annotation { "Feature Type Name" : "Feature", "Feature Type Description" : "" }
export const myFeature = defineFeature(function(context is Context, id is Id, definition is map)
    precondition{}
    {
        {
            var Q0;
            Q0=qCreatedBy(makeId("Top.planeOp"),FACE);
            var sketch = newSketch(context, id + "F0", { "sketchPlane" : qUnion([Q0])});
            skLineSegment(sketch, "E0.bottom", {"start": v(-43.82, 31.44) * mm, "end": v(43.82, 31.44) * mm});
            skLineSegment(sketch, "E0.top", {"start": v(-43.82, -31.44) * mm, "end": v(43.82, -31.44) * mm});
            skLineSegment(sketch, "E0.left", {"start": v(-48.82, 26.44) * mm, "end": v(-48.82, -26.44) * mm});
            skLineSegment(sketch, "E0.right", {"start": v(48.82, 26.44) * mm, "end": v(48.82, -26.44) * mm});
            skPoint(sketch, "E0.middle", {"position": v(0, 0) * mm});
            skPoint(sketch, "E1.visualSharp", {"position": v(-48.82, 31.44) * mm});
            skArc(sketch, "E1.filletArc", {"start": v(-43.82, 31.44) * mm, "mid": v(-47.36, 29.97) * mm, "end": v(-48.82, 26.44) * mm});
            skPoint(sketch, "E2.visualSharp", {"position": v(-48.82, -31.44) * mm});
            skArc(sketch, "E2.filletArc", {"start": v(-48.82, -26.44) * mm, "mid": v(-47.36, -29.97) * mm, "end": v(-43.82, -31.44) * mm});
            skPoint(sketch, "E3.visualSharp", {"position": v(48.82, -31.44) * mm});
            skArc(sketch, "E3.filletArc", {"start": v(43.82, -31.44) * mm, "mid": v(47.36, -29.97) * mm, "end": v(48.82, -26.44) * mm});
            skPoint(sketch, "E4.visualSharp", {"position": v(48.82, 31.44) * mm});
            skArc(sketch, "E4.filletArc", {"start": v(48.82, 26.44) * mm, "mid": v(47.36, 29.97) * mm, "end": v(43.82, 31.44) * mm});
            skCircle(sketch, "E5", {"center": v(42.82, 25.44) * mm, "radius": 2.5 * mm});
            skCircle(sketch, "E6.MirrorC", {"center": v(-42.82, 25.44) * mm, "radius": 2.5 * mm});
            skSolve(sketch);
        }
        {
            var Q0;
            Q0 = qSketchRegion(id + "F0", true);
            extrude(context, id + "F1", {"entities" : qUnion([Q0]), "depth" : 3 * mm});
        }
        {
            var Q0;
            Q0=qCreatedBy(makeId("Top.planeOp"),FACE);
            var sketch = newSketch(context, id + "F2", { "sketchPlane" : qUnion([Q0])});
            skFitSpline(sketch, "E7", {"points": [v(21.62, 6.78) * mm, v(22.6, 7.89) * mm, v(23.46, 8.32) * mm, v(24.65, 8.86) * mm, v(25.98, 9.48) * mm, v(26.54, 10.02) * mm, v(26.92, 10.91) * mm, v(26.9, 11.43) * mm, v(26.65, 11.21) * mm, v(26.52, 11.4) * mm, v(27.08, 12.22) * mm, v(27.82, 12.98) * mm, v(27.9, 13.86) * mm, v(27.94, 15.05) * mm, v(27.94, 17.07) * mm, v(27.87, 17.63) * mm, v(27.9, 19.67) * mm, v(27.9, 21.6) * mm, v(28.27, 21.58) * mm, v(29.33, 20.23) * mm, v(31.93, 16.98) * mm, v(33.27, 15.72) * mm, v(34.13, 15.63) * mm, v(34.94, 16.39) * mm, v(36.1, 18.95) * mm, v(38, 21.24) * mm, v(39.47, 22.14) * mm, v(40.25, 21.06) * mm, v(40.25, 16.6) * mm, v(40, 15.33) * mm, v(40.39, 12.67) * mm, v(40.48, 11.3) * mm, v(40.1, 10.54) * mm, v(40.46, 9.74) * mm, v(41.2, 8.63) * mm, v(41.19, 5.67) * mm, v(40.78, 4.58) * mm, v(40.75, 3.15) * mm, v(41.2, 1.54) * mm, v(41.32, 0) * mm, v(41.23, -0.83) * mm, v(41.5, -3.03) * mm, v(42.07, -4.62) * mm, v(41.3, -4.92) * mm, v(40.39, -4.74) * mm, v(39.23, -5.24) * mm, v(38.64, -5.83) * mm, v(36.5, -6.12) * mm, v(35.75, -6.76) * mm, v(33.7, -6.83) * mm, v(32.03, -7.03) * mm, v(28.7, -5.96) * mm, v(25.46, -5.24) * mm, v(24.82, -4.5) * mm, v(25.03, -3.28) * mm, v(25.66, -1) * mm, v(26.16, 0.95) * mm, v(25.91, 1.17) * mm, v(25.53, 0.8) * mm, v(24.3, 1.01) * mm, v(24.35, 2.74) * mm, v(24.85, 3.6) * mm, v(24.8, 3.92) * mm, v(23.19, 3.92) * mm, v(22.07, 5.6) * mm, v(21.73, 5.85) * mm, v(21.62, 6.78) * mm]});
            skSolve(sketch);
        }
        {
            var Q0;
            Q0 = qSketchRegion(id + "F2", true);
            extrude(context, id + "F3", {"entities" : qUnion([Q0]), "depth" : 4 * mm});
        }
        {
            var Q0;
            Q0=qCreatedBy(makeId("Top.planeOp"),FACE);
            var sketch = newSketch(context, id + "F4", { "sketchPlane" : qUnion([Q0])});
            skText(sketch, "E8", { "text": "PO VSTUPE\nSA TI HNED\nBUDEM VENOVAT", "fontName": "AllertaStencil-Regular.ttf"});
            const initialGuessF4  = {"E8": [-0.04382, 0.0064, 1, 0, 0.00703]};
            skSetInitialGuess(sketch, initialGuessF4);
            skSolve(sketch);
        }
        {
            var Q0;
            Q0 = qSketchRegion(id + "F4", true);
            extrude(context, id + "F5", {"entities" : qUnion([Q0]), "operationType" : NewBodyOperationType.REMOVE, "depth" : 25 * mm});
        }
        {
            var Q0;
            Q0=makeQuery(id+"F3.opExtrude","SWEPT_BODY",BODY,{"disambiguationData":[OSD([sQuery(id+"F2.wireOp",EDGE,"E7")])]});
            transform(context, id + "F6", {"entities" : qUnion([Q0]), "transformType" : TransformType.TRANSLATION_3D, "dx" : 0 * mm, "dy" : 0 * mm, "dz" : 0 * mm, "makeCopy" : true});
        }
        {
            var Q0;
            Q0=makeQuery(id+"F6.opPattern","COPY",BODY,{"derivedFrom":makeQuery(id+"F3.opExtrude","SWEPT_BODY",BODY,{"disambiguationData":[OSD([sQuery(id+"F2.wireOp",EDGE,"E7")])]}),"instanceName":"1"});
            var Q1;
            Q1=makeQuery(id+"F1.opExtrude","CAP_EDGE",EDGE,{"disambiguationData":[OSD([sQuery(id+"F0.wireOp",EDGE,"E0.right")])],"isStart":false});
            transform(context, id + "F7", {"entities" : qUnion([Q0]), "transformType" : TransformType.ROTATION, "transformAxis" : qUnion([Q1]), "angle" : 1.7 * degree, "oppositeDirection" : true, "makeCopy" : false});
        }
        {
            var Q0;
            Q0=qCreatedBy(makeId("Top.planeOp"),FACE);
            var sketch = newSketch(context, id + "F8", { "sketchPlane" : qUnion([Q0])});
            skLineSegment(sketch, "E9.bottom", {"start": v(-42.32, 29.94) * mm, "end": v(42.32, 29.94) * mm});
            skLineSegment(sketch, "E9.top", {"start": v(-42.32, -29.94) * mm, "end": v(42.32, -29.94) * mm});
            skLineSegment(sketch, "E9.left", {"start": v(-47.32, 24.94) * mm, "end": v(-47.32, -24.94) * mm});
            skLineSegment(sketch, "E9.right", {"start": v(47.32, 24.94) * mm, "end": v(47.32, -24.94) * mm});
            skPoint(sketch, "E9.middle", {"position": v(0, 0) * mm});
            skPoint(sketch, "E10.visualSharp", {"position": v(-47.32, 29.94) * mm});
            skArc(sketch, "E10.filletArc", {"start": v(-42.32, 29.94) * mm, "mid": v(-45.86, 28.47) * mm, "end": v(-47.32, 24.94) * mm});
            skPoint(sketch, "E11.visualSharp", {"position": v(-47.32, -29.94) * mm});
            skArc(sketch, "E11.filletArc", {"start": v(-47.32, -24.94) * mm, "mid": v(-45.86, -28.47) * mm, "end": v(-42.32, -29.94) * mm});
            skPoint(sketch, "E12.visualSharp", {"position": v(47.32, -29.94) * mm});
            skArc(sketch, "E12.filletArc", {"start": v(42.32, -29.94) * mm, "mid": v(45.86, -28.47) * mm, "end": v(47.32, -24.94) * mm});
            skPoint(sketch, "E13.visualSharp", {"position": v(47.32, 29.94) * mm});
            skArc(sketch, "E13.filletArc", {"start": v(47.32, 24.94) * mm, "mid": v(45.86, 28.47) * mm, "end": v(42.32, 29.94) * mm});
            skLineSegment(sketch, "E14.bottom", {"start": v(-41.32, 28.94) * mm, "end": v(41.32, 28.94) * mm});
            skLineSegment(sketch, "E14.top", {"start": v(-41.32, -28.94) * mm, "end": v(41.32, -28.94) * mm});
            skLineSegment(sketch, "E14.left", {"start": v(-46.32, 23.94) * mm, "end": v(-46.32, -23.94) * mm});
            skLineSegment(sketch, "E14.right", {"start": v(46.32, 23.94) * mm, "end": v(46.32, -23.94) * mm});
            skPoint(sketch, "E15.visualSharp", {"position": v(-46.32, 28.94) * mm});
            skArc(sketch, "E15.filletArc", {"start": v(-41.32, 28.94) * mm, "mid": v(-44.86, 27.47) * mm, "end": v(-46.32, 23.94) * mm});
            skPoint(sketch, "E16.visualSharp", {"position": v(-46.32, -28.94) * mm});
            skArc(sketch, "E16.filletArc", {"start": v(-46.32, -23.94) * mm, "mid": v(-44.86, -27.47) * mm, "end": v(-41.32, -28.94) * mm});
            skPoint(sketch, "E17.visualSharp", {"position": v(46.32, -28.94) * mm});
            skArc(sketch, "E17.filletArc", {"start": v(41.32, -28.94) * mm, "mid": v(44.86, -27.47) * mm, "end": v(46.32, -23.94) * mm});
            skPoint(sketch, "E18.visualSharp", {"position": v(46.32, 28.94) * mm});
            skArc(sketch, "E18.filletArc", {"start": v(46.32, 23.94) * mm, "mid": v(44.86, 27.47) * mm, "end": v(41.32, 28.94) * mm});
            skSolve(sketch);
        }
        {
            var Q0;
            Q0 = qSketchRegion(id + "F8", true);
            extrude(context, id + "F9", {"entities" : qUnion([Q0]), "depth" : 4 * mm});
        }
        {
            var Q0;
            Q0=qCreatedBy(makeId("Top.planeOp"),FACE);
            var sketch = newSketch(context, id + "F10", { "sketchPlane" : qUnion([Q0])});
            skLineSegment(sketch, "E19.bottom", {"start": v(-44.14, 16.07) * mm, "end": v(11.85, 16.07) * mm});
            skLineSegment(sketch, "E19.top", {"start": v(-44.14, -8.77) * mm, "end": v(11.85, -8.77) * mm});
            skLineSegment(sketch, "E19.left", {"start": v(-44.14, 16.07) * mm, "end": v(-44.14, -8.77) * mm});
            skLineSegment(sketch, "E19.right", {"start": v(11.85, 16.07) * mm, "end": v(11.85, -8.77) * mm});
            skLineSegment(sketch, "E20.bottom", {"start": v(-44.14, -8.77) * mm, "end": v(43.39, -8.77) * mm});
            skLineSegment(sketch, "E20.top", {"start": v(-44.14, -22.15) * mm, "end": v(43.39, -22.15) * mm});
            skLineSegment(sketch, "E20.left", {"start": v(-44.14, -8.77) * mm, "end": v(-44.14, -22.15) * mm});
            skLineSegment(sketch, "E20.right", {"start": v(43.39, -8.77) * mm, "end": v(43.39, -22.15) * mm});
            skSolve(sketch);
        }
        {
            var Q0;
            Q0 = qSketchRegion(id + "F10", true);
            extrude(context, id + "F11", {"entities" : qUnion([Q0]), "operationType" : NewBodyOperationType.ADD, "depth" : 1 * mm});
        }
    });